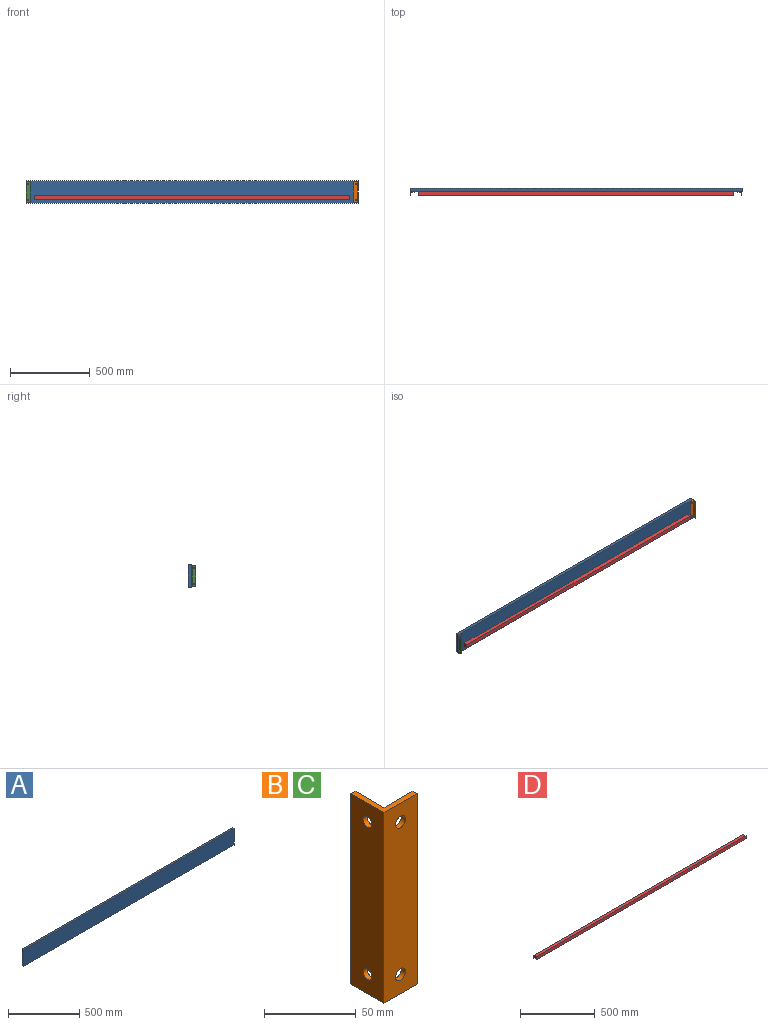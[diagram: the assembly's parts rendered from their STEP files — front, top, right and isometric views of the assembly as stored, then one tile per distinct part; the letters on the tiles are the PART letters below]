
ASSEMBLY  parts=4 mates=3
PART A: 6 faces, bbox 2082.8x19.1x139.7 mm
  f0: plane 2082.8x19.05mm, normal (0,0,1), area 39677.3mm2, adj f1,f3,f4,f5
  f1: plane 139.7x19.05mm, normal (-1,0,0), area 2661.3mm2, adj f0,f2,f4,f5
  f2: plane 2082.8x19.05mm, normal (0,0,-1), area 39677.3mm2, adj f1,f3,f4,f5
  f3: plane 139.7x19.05mm, normal (1,0,0), area 2661.3mm2, adj f0,f2,f4,f5
  f4: plane 2082.8x139.7mm, normal (0,1,0), area 290967.2mm2, adj f0,f1,f2,f3
  f5: plane 2082.8x139.7mm, normal (0,-1,0), area 290967.2mm2, adj f0,f1,f2,f3
PART B: 12 faces, bbox 25.4x25.4x127 mm
  f0: plane 127x22.23mm, normal (0,1,0), area 2730.3mm2, adj f3,f5,f6,f7,f10,f11
  f1: plane 127x25.4mm, normal (0,-1,0), area 3133.5mm2, adj f2,f5,f6,f7,f10,f11
  f2: plane 127x25.4mm, normal (-1,0,0), area 3150.3mm2, adj f1,f4,f6,f7,f8,f9
  f3: plane 127x22.23mm, normal (1,0,0), area 2747.1mm2, adj f0,f4,f6,f7,f8,f9
  f4: plane 127x3.18mm, normal (0,1,0), area 403.2mm2, adj f2,f3,f6,f7
  f5: plane 127x3.18mm, normal (1,0,0), area 403.2mm2, adj f0,f1,f6,f7
  f6: plane 25.4x25.4mm, normal (0,0,-1), area 151.2mm2, adj f0,f1,f2,f3,f4,f5
  f7: plane 25.4x25.4mm, normal (0,0,1), area 151.2mm2, adj f0,f1,f2,f3,f4,f5
  f8: cylinder r=3.47mm len=6.93mm, axis (1,0,0), area 69.1mm2, adj f2,f3
  f9: cylinder r=3.47mm len=6.93mm, axis (1,0,0), area 69.1mm2, adj f2,f3
  f10: cylinder r=3.83mm len=7.67mm, axis (0,1,0), area 76.5mm2, adj f0,f1
  f11: cylinder r=3.83mm len=7.67mm, axis (0,1,0), area 76.5mm2, adj f0,f1
PART C: same geometry as B
PART D: 6 faces, bbox 1981.2x25.4x25.4 mm
  f0: plane 1981.2x25.4mm, normal (0,0,-1), area 50322.5mm2, adj f1,f3,f4,f5
  f1: plane 1981.2x25.4mm, normal (0,1,0), area 50322.5mm2, adj f0,f2,f4,f5
  f2: plane 1981.2x25.4mm, normal (0,0,1), area 50322.5mm2, adj f1,f3,f4,f5
  f3: plane 1981.2x25.4mm, normal (0,-1,0), area 50322.5mm2, adj f0,f2,f4,f5
  f4: plane 25.4x25.4mm, normal (1,0,0), area 645.2mm2, adj f0,f1,f2,f3
  f5: plane 25.4x25.4mm, normal (-1,0,0), area 645.2mm2, adj f0,f1,f2,f3
PLACE A t=(-454.26,998.19,-294.86)mm
PLACE B rot(axis=(0,0,1),180deg) t=(1685.8,-534.88,-275.81)mm
PLACE C rot(axis=(1,0,0),180deg) t=(-511.53,-534.88,-13.74)mm
PLACE D rot(axis=(-1,0,0),90deg) t=(-403.46,201.13,-1392.58)mm
MATE fastened B.f1 <-> A.f5  axis (0,1,0) through (1628.54,191.74,-81.28)mm
MATE fastened C.f1 <-> A.f5  axis (0,1,0) through (-454.26,191.74,-208.28)mm
MATE fastened D.f2 <-> A.f5  axis (0,1,0) through (587.14,191.74,-189.23)mm
